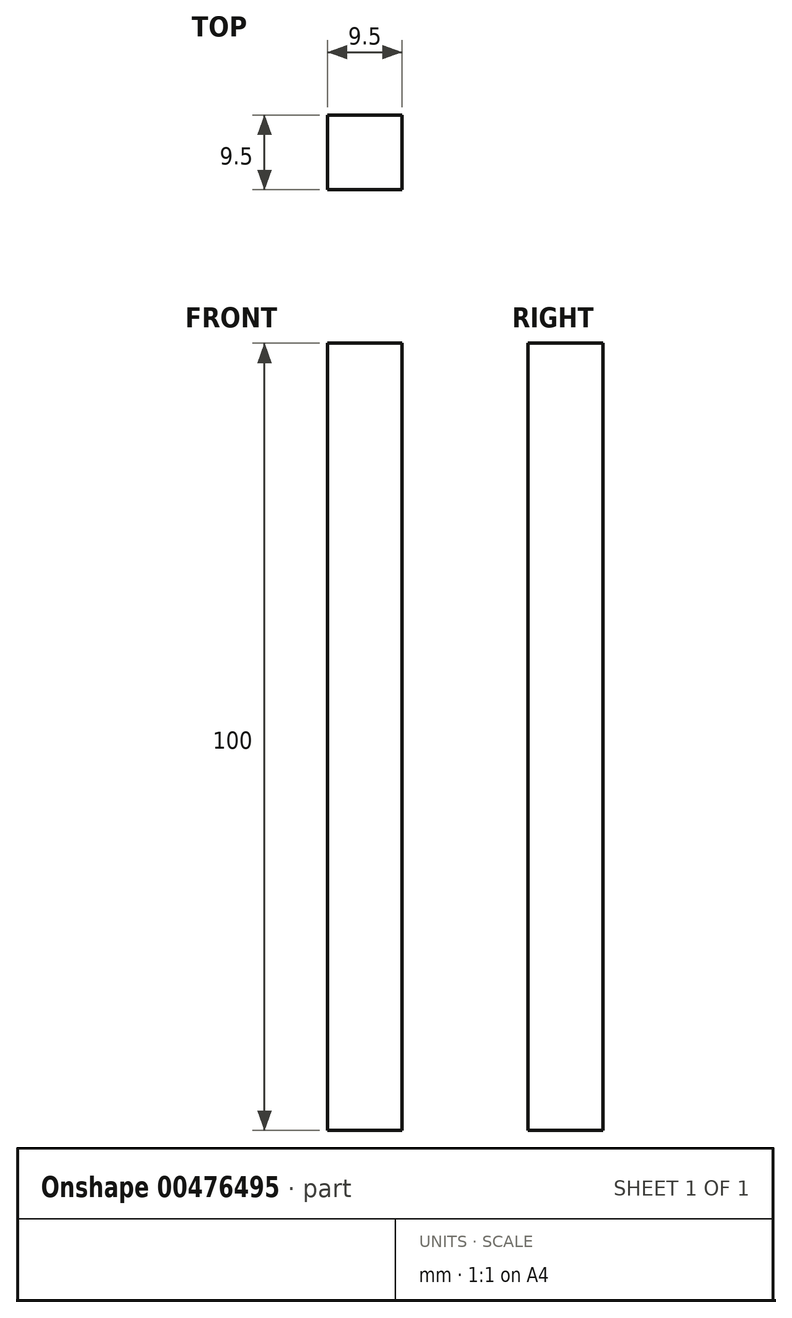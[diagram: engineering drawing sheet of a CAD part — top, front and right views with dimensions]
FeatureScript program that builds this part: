
annotation { "Feature Type Name" : "Feature", "Feature Type Description" : "" }
export const myFeature = defineFeature(function(context is Context, id is Id, definition is map)
    precondition{}
    {
        {
            var Q0;
            Q0=qCreatedBy(makeId("Top.planeOp"),FACE);
            var sketch = newSketch(context, id + "F0", { "sketchPlane" : qUnion([Q0])});
            skLineSegment(sketch, "E0.bottom", {"start": v(-6.36, 3.96) * mm, "end": v(3.14, 3.96) * mm});
            skLineSegment(sketch, "E0.top", {"start": v(-6.36, -5.54) * mm, "end": v(3.14, -5.54) * mm});
            skLineSegment(sketch, "E0.left", {"start": v(-6.36, 3.96) * mm, "end": v(-6.36, -5.54) * mm});
            skLineSegment(sketch, "E0.right", {"start": v(3.14, 3.96) * mm, "end": v(3.14, -5.54) * mm});
            skSolve(sketch);
        }
        {
            var Q0;
            Q0=makeQuery(id+"F0.imprint","IMPRINT",FACE,{"disambiguationData":[TD([[makeQuery(id+"F0.imprint","IMPRINT",EDGE,{"derivedFrom":sQuery(id+"F0.wireOp",EDGE,"E0.bottom")}),-1.0]])]});
            extrude(context, id + "F1", {"entities" : qUnion([Q0]), "depth" : 100 * mm});
        }
    });
